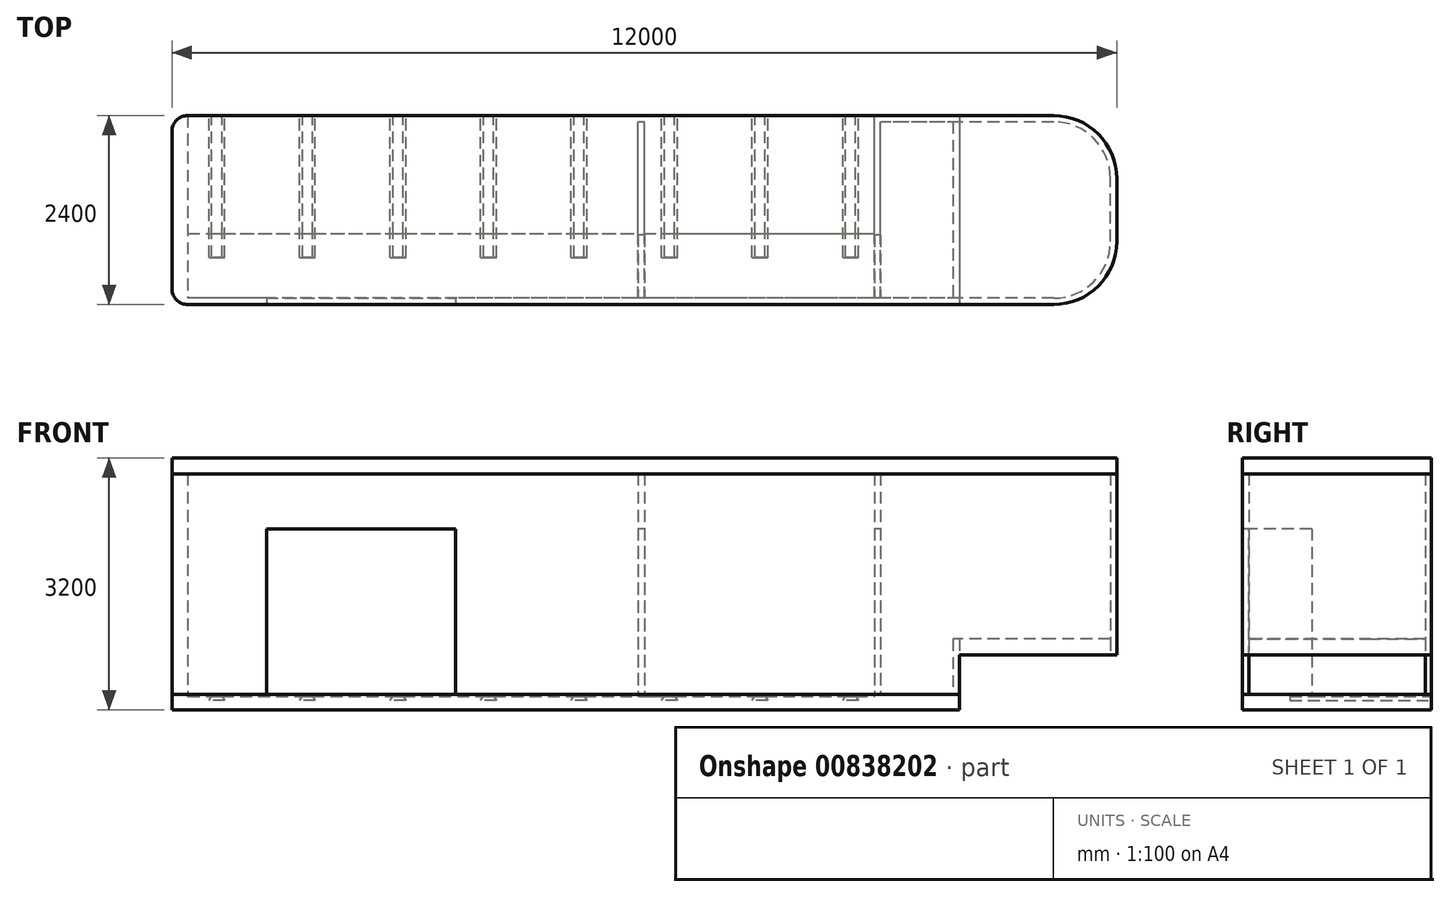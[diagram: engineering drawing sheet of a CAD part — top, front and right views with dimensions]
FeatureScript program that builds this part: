
annotation { "Feature Type Name" : "Feature", "Feature Type Description" : "" }
export const myFeature = defineFeature(function(context is Context, id is Id, definition is map)
    precondition{}
    {
        {
            var Q0;
            Q0=qCreatedBy(makeId("Top.planeOp"),FACE);
            var sketch = newSketch(context, id + "F0", { "sketchPlane" : qUnion([Q0])});
            skLineSegment(sketch, "E0.bottom", {"start": v(5200, -1200) * mm, "end": v(-5800, -1200) * mm});
            skLineSegment(sketch, "E0.top", {"start": v(5200, 1200) * mm, "end": v(2920, 1200) * mm});
            skLineSegment(sketch, "E0.left", {"start": v(6000, -400) * mm, "end": v(6000, 400) * mm});
            skLineSegment(sketch, "E0.right", {"start": v(-6000, -1000) * mm, "end": v(-6000, 1000) * mm});
            skPoint(sketch, "E0.middle", {"position": v(0, 0) * mm});
            skPoint(sketch, "E1.visualSharp", {"position": v(6000, 1200) * mm});
            skArc(sketch, "E1.filletArc", {"start": v(6000, 400) * mm, "mid": v(5765.69, 965.69) * mm, "end": v(5200, 1200) * mm});
            skPoint(sketch, "E2.visualSharp", {"position": v(6000, -1200) * mm});
            skArc(sketch, "E2.filletArc", {"start": v(5200, -1200) * mm, "mid": v(5765.69, -965.69) * mm, "end": v(6000, -400) * mm});
            skPoint(sketch, "E3.visualSharp", {"position": v(-6000, -1200) * mm});
            skArc(sketch, "E3.filletArc", {"start": v(-6000, -1000) * mm, "mid": v(-5941.42, -1141.42) * mm, "end": v(-5800, -1200) * mm});
            skPoint(sketch, "E4.visualSharp", {"position": v(-6000, 1200) * mm});
            skArc(sketch, "E4.filletArc", {"start": v(-5800, 1200) * mm, "mid": v(-5941.42, 1141.42) * mm, "end": v(-6000, 1000) * mm});
            skLineSegment(sketch, "E5", {"start": v(3000, -1120) * mm, "end": v(3000, 1120) * mm});
            skArc(sketch, "E6.0", {"start": v(5200, -1120) * mm, "mid": v(5709.12, -909.12) * mm, "end": v(5920, -400) * mm});
            skArc(sketch, "E6.1", {"start": v(5920, 400) * mm, "mid": v(5709.12, 909.12) * mm, "end": v(5200, 1120) * mm});
            skLineSegment(sketch, "E6.2", {"start": v(5200, 1120) * mm, "end": v(3000, 1120) * mm});
            skLineSegment(sketch, "E6.3", {"start": v(5920, -400) * mm, "end": v(5920, 400) * mm});
            skLineSegment(sketch, "E6.5", {"start": v(5200, -1120) * mm, "end": v(-5800, -1120) * mm});
            skLineSegment(sketch, "E7", {"start": v(-5800, 1200) * mm, "end": v(-5800, -1120) * mm});
            skLineSegment(sketch, "E8.0", {"start": v(2920, -1120) * mm, "end": v(2920, 1200) * mm});
            skLineSegment(sketch, "E9.0", {"start": v(0, -1120) * mm, "end": v(0, 1120) * mm});
            skLineSegment(sketch, "E10.0", {"start": v(-80, -1120) * mm, "end": v(-80, 1120) * mm});
            skLineSegment(sketch, "E11.trimOffspring", {"start": v(0, 1120) * mm, "end": v(-80, 1120) * mm});
            skLineSegment(sketch, "E12", {"start": v(-5800, 1200) * mm, "end": v(2920, 1200) * mm});
            skLineSegment(sketch, "E13.0", {"start": v(-5800, -300) * mm, "end": v(2920, -300) * mm});
            skLineSegment(sketch, "E14", {"start": v(4000, 1200) * mm, "end": v(4000, -1200) * mm});
            skLineSegment(sketch, "E15.0", {"start": v(3920, 1120) * mm, "end": v(3920, -1120) * mm});
            skSolve(sketch);
        }
        {
            var Q0;
            Q0=makeQuery(id+"F0.imprint","IMPRINT",FACE,{"disambiguationData":[TD([[makeQuery(id+"F0.imprint","IMPRINT",EDGE,{"derivedFrom":sQuery(id+"F0.wireOp",EDGE,"E0.bottom")}),-1.0]])]});
            var Q1;
            {var subQ0=sQuery(id+"F0.wireOp",EDGE,"E9.0");Q1=makeQuery(id+"F0.imprint","IMPRINT",FACE,{"disambiguationData":[TD([[makeQuery(id+"F0.imprint","IMPRINT",EDGE,{"derivedFrom":subQ0}),1.0]])]});}
            var Q2;
            {var subQ1=sQuery(id+"F0.wireOp",EDGE,"E5");Q2=makeQuery(id+"F0.imprint","IMPRINT",FACE,{"disambiguationData":[TD([[makeQuery(id+"F0.imprint","IMPRINT",EDGE,{"derivedFrom":subQ1}),1.0]])]});}
            var Q3;
            Q3=makeQuery(id+"F0.imprint","IMPRINT",FACE,{"disambiguationData":[TD([[makeQuery(id+"F0.imprint","IMPRINT",EDGE,{"derivedFrom":sQuery(id+"F0.wireOp",EDGE,"E0.right")}),-1.0]])]});
            extrude(context, id + "F1", {"entities" : qUnion([Q0, Q1, Q2, Q3]), "depth" : 2800 * mm, "offsetDistance" : 25 * mm});
        }
        {
            var Q0;
            {var subQ1=sQuery(id+"F0.wireOp",EDGE,"E5");Q0=makeQuery(id+"F0.imprint","IMPRINT",FACE,{"disambiguationData":[TD([[makeQuery(id+"F0.imprint","IMPRINT",EDGE,{"derivedFrom":subQ1}),-1.0]])]});}
            var Q1;
            {var subQ0=sQuery(id+"F0.wireOp",EDGE,"E9.0");Q1=makeQuery(id+"F0.imprint","IMPRINT",FACE,{"disambiguationData":[TD([[makeQuery(id+"F0.imprint","IMPRINT",EDGE,{"derivedFrom":subQ0}),1.0]])]});}
            var Q2;
            {var subQ0=sQuery(id+"F0.wireOp",EDGE,"E7");var subQ1=sQuery(id+"F0.wireOp",EDGE,"E6.5");var subQ2=makeQuery(id+"F0.imprint","INTERSECT",VERTEX,{"derivedFrom":[subQ1,subQ0]});Q2=makeQuery(id+"F0.imprint","IMPRINT",FACE,{"disambiguationData":[TD([[makeQuery(id+"F0.imprint","IMPRINT",EDGE,{"disambiguationData":[TD([[subQ2,1.0]])],"derivedFrom":subQ1}),-1.0]])]});}
            var Q3;
            {var subQ0=sQuery(id+"F0.wireOp",EDGE,"E8.0");var subQ1=sQuery(id+"F0.wireOp",EDGE,"E6.5");var subQ2=makeQuery(id+"F0.imprint","INTERSECT",VERTEX,{"derivedFrom":[subQ1,subQ0]});Q3=makeQuery(id+"F0.imprint","IMPRINT",FACE,{"disambiguationData":[TD([[makeQuery(id+"F0.imprint","IMPRINT",EDGE,{"disambiguationData":[TD([[subQ2,-1.0]])],"derivedFrom":subQ1}),-1.0]])]});}
            var Q4;
            {var subQ0=sQuery(id+"F0.wireOp",EDGE,"E11.trimOffspring");Q4=makeQuery(id+"F0.imprint","IMPRINT",FACE,{"disambiguationData":[TD([[makeQuery(id+"F0.imprint","IMPRINT",EDGE,{"derivedFrom":subQ0}),-1.0]])]});}
            var Q5;
            Q5=makeQuery(id+"F0.imprint","IMPRINT",FACE,{"disambiguationData":[TD([[makeQuery(id+"F0.imprint","IMPRINT",EDGE,{"derivedFrom":sQuery(id+"F0.wireOp",EDGE,"E0.right")}),-1.0]])]});
            var Q6;
            {var subQ1=sQuery(id+"F0.wireOp",EDGE,"E5");Q6=makeQuery(id+"F0.imprint","IMPRINT",FACE,{"disambiguationData":[TD([[makeQuery(id+"F0.imprint","IMPRINT",EDGE,{"derivedFrom":subQ1}),1.0]])]});}
            var Q7;
            {var subQ0=sQuery(id+"F0.wireOp",EDGE,"E15.0");Q7=makeQuery(id+"F0.imprint","IMPRINT",FACE,{"disambiguationData":[TD([[makeQuery(id+"F0.imprint","IMPRINT",EDGE,{"derivedFrom":subQ0}),1.0]])]});}
            extrude(context, id + "F2", {"entities" : qUnion([Q0, Q1, Q2, Q3, Q4, Q5, Q6, Q7]), "oppositeDirection" : true, "depth" : 200 * mm, "offsetDistance" : 25 * mm});
        }
        {
            var Q0;
            Q0=makeQuery(id+"F1.opExtrude","SWEPT_FACE",FACE,{"disambiguationData":[OSD([sQuery(id+"F0.wireOp",EDGE,"E0.bottom")])]});
            var sketch = newSketch(context, id + "F3", { "sketchPlane" : qUnion([Q0])});
            skLineSegment(sketch, "E16.bottom", {"start": v(-4800, 0) * mm, "end": v(-2400, 0) * mm});
            skLineSegment(sketch, "E16.top", {"start": v(-4800, 2100) * mm, "end": v(-2400, 2100) * mm});
            skLineSegment(sketch, "E16.left", {"start": v(-4800, 0) * mm, "end": v(-4800, 2100) * mm});
            skLineSegment(sketch, "E16.right", {"start": v(-2400, 0) * mm, "end": v(-2400, 2100) * mm});
            skSolve(sketch);
        }
        {
            var Q0;
            Q0=makeQuery(id+"F3.imprint","IMPRINT",FACE,{"disambiguationData":[TD([[makeQuery(id+"F3.imprint","IMPRINT",EDGE,{"derivedFrom":sQuery(id+"F3.wireOp",EDGE,"E16.bottom")}),-1.0]])]});
            extrude(context, id + "F4", {"entities" : qUnion([Q0]), "operationType" : NewBodyOperationType.REMOVE, "oppositeDirection" : true, "depth" : 1454.27 * mm, "offsetDistance" : 25 * mm});
        }
        {
            var Q0;
            Q0=makeQuery(id+"F1.opExtrude","SWEPT_FACE",FACE,{"disambiguationData":[OSD([sQuery(id+"F0.wireOp",EDGE,"E10.0")])]});
            var sketch = newSketch(context, id + "F5", { "sketchPlane" : qUnion([Q0])});
            skLineSegment(sketch, "E17.bottom", {"start": v(320, 2100) * mm, "end": v(1120, 2100) * mm});
            skLineSegment(sketch, "E17.top", {"start": v(320, 0) * mm, "end": v(1120, 0) * mm});
            skLineSegment(sketch, "E17.left", {"start": v(320, 2100) * mm, "end": v(320, 0) * mm});
            skLineSegment(sketch, "E17.right", {"start": v(1120, 2100) * mm, "end": v(1120, 0) * mm});
            skSolve(sketch);
        }
        {
            var Q0;
            Q0=makeQuery(id+"F5.imprint","IMPRINT",FACE,{"disambiguationData":[TD([[makeQuery(id+"F5.imprint","IMPRINT",EDGE,{"derivedFrom":sQuery(id+"F5.wireOp",EDGE,"E17.bottom")}),-1.0]])]});
            extrude(context, id + "F6", {"entities" : qUnion([Q0]), "operationType" : NewBodyOperationType.REMOVE, "oppositeDirection" : true, "depth" : 3837 * mm, "offsetDistance" : 25 * mm});
        }
        {
            var Q0;
            {var subQ0=sQuery(id+"F0.wireOp",EDGE,"E11.trimOffspring");Q0=makeQuery(id+"F0.imprint","IMPRINT",FACE,{"disambiguationData":[TD([[makeQuery(id+"F0.imprint","IMPRINT",EDGE,{"derivedFrom":subQ0}),-1.0]])]});}
            extrude(context, id + "F7", {"entities" : qUnion([Q0]), "operationType" : NewBodyOperationType.REMOVE, "oppositeDirection" : true, "depth" : 30 * mm, "offsetDistance" : 25 * mm});
        }
        {
            var Q0;
            Q0=makeQuery(id+"F2.opExtrude","SWEPT_FACE",FACE,{"disambiguationData":[OSD([sQuery(id+"F0.wireOp",EDGE,"E0.top"),sQuery(id+"F0.wireOp",EDGE,"E12")])]});
            var sketch = newSketch(context, id + "F8", { "sketchPlane" : qUnion([Q0])});
            skLineSegment(sketch, "E18", {"start": v(-2920, -200) * mm, "end": v(5800, -200) * mm});
            skLineSegment(sketch, "E19", {"start": v(-2920, -200) * mm, "end": v(-2920, -30) * mm});
            skLineSegment(sketch, "E20", {"start": v(-2920, -30) * mm, "end": v(5800, -30) * mm});
            skLineSegment(sketch, "E21", {"start": v(5800, -30) * mm, "end": v(5800, -200) * mm});
            skLineSegment(sketch, "E22", {"start": v(-2684.32, -30) * mm, "end": v(-2720, -80) * mm});
            skLineSegment(sketch, "E23", {"start": v(-2720, -80) * mm, "end": v(-2520, -80) * mm});
            skLineSegment(sketch, "E24", {"start": v(-2520, -80) * mm, "end": v(-2555.68, -30) * mm});
            skLineSegment(sketch, "E25.1.0.0", {"start": v(-1534.32, -30) * mm, "end": v(-1570, -80) * mm});
            skLineSegment(sketch, "E25.1.0.1", {"start": v(-1570, -80) * mm, "end": v(-1370, -80) * mm});
            skLineSegment(sketch, "E25.1.0.2", {"start": v(-1370, -80) * mm, "end": v(-1405.68, -30) * mm});
            skLineSegment(sketch, "E25.2.0.0", {"start": v(-384.32, -30) * mm, "end": v(-420, -80) * mm});
            skLineSegment(sketch, "E25.2.0.1", {"start": v(-420, -80) * mm, "end": v(-220, -80) * mm});
            skLineSegment(sketch, "E25.2.0.2", {"start": v(-220, -80) * mm, "end": v(-255.68, -30) * mm});
            skLineSegment(sketch, "E25.3.0.0", {"start": v(765.68, -30) * mm, "end": v(730, -80) * mm});
            skLineSegment(sketch, "E25.3.0.1", {"start": v(730, -80) * mm, "end": v(930, -80) * mm});
            skLineSegment(sketch, "E25.3.0.2", {"start": v(930, -80) * mm, "end": v(894.32, -30) * mm});
            skLineSegment(sketch, "E25.4.0.0", {"start": v(1915.68, -30) * mm, "end": v(1880, -80) * mm});
            skLineSegment(sketch, "E25.4.0.1", {"start": v(1880, -80) * mm, "end": v(2080, -80) * mm});
            skLineSegment(sketch, "E25.4.0.2", {"start": v(2080, -80) * mm, "end": v(2044.32, -30) * mm});
            skLineSegment(sketch, "E25.5.0.0", {"start": v(3065.68, -30) * mm, "end": v(3030, -80) * mm});
            skLineSegment(sketch, "E25.5.0.1", {"start": v(3030, -80) * mm, "end": v(3230, -80) * mm});
            skLineSegment(sketch, "E25.5.0.2", {"start": v(3230, -80) * mm, "end": v(3194.32, -30) * mm});
            skLineSegment(sketch, "E25.6.0.0", {"start": v(4215.68, -30) * mm, "end": v(4180, -80) * mm});
            skLineSegment(sketch, "E25.6.0.1", {"start": v(4180, -80) * mm, "end": v(4380, -80) * mm});
            skLineSegment(sketch, "E25.6.0.2", {"start": v(4380, -80) * mm, "end": v(4344.32, -30) * mm});
            skLineSegment(sketch, "E25.7.0.0", {"start": v(5365.68, -30) * mm, "end": v(5330, -80) * mm});
            skLineSegment(sketch, "E25.7.0.1", {"start": v(5330, -80) * mm, "end": v(5530, -80) * mm});
            skLineSegment(sketch, "E25.7.0.2", {"start": v(5530, -80) * mm, "end": v(5494.32, -30) * mm});
            skLineSegment(sketch, "E25.direction1", {"start": v(-2720, -80) * mm, "end": v(-1570, -80) * mm, "construction": true});
            skSolve(sketch);
        }
        {
            var Q0;
            {var subQ0=sQuery(id+"F8.wireOp",EDGE,"E22");Q0=makeQuery(id+"F8.imprint","IMPRINT",FACE,{"disambiguationData":[TD([[makeQuery(id+"F8.imprint","IMPRINT",EDGE,{"derivedFrom":subQ0}),1.0]])]});}
            var Q1;
            {var subQ0=sQuery(id+"F8.wireOp",EDGE,"E25.1.0.0");Q1=makeQuery(id+"F8.imprint","IMPRINT",FACE,{"disambiguationData":[TD([[makeQuery(id+"F8.imprint","IMPRINT",EDGE,{"derivedFrom":subQ0}),1.0]])]});}
            var Q2;
            {var subQ0=sQuery(id+"F8.wireOp",EDGE,"E25.2.0.0");Q2=makeQuery(id+"F8.imprint","IMPRINT",FACE,{"disambiguationData":[TD([[makeQuery(id+"F8.imprint","IMPRINT",EDGE,{"derivedFrom":subQ0}),1.0]])]});}
            var Q3;
            {var subQ0=sQuery(id+"F8.wireOp",EDGE,"E25.4.0.0");Q3=makeQuery(id+"F8.imprint","IMPRINT",FACE,{"disambiguationData":[TD([[makeQuery(id+"F8.imprint","IMPRINT",EDGE,{"derivedFrom":subQ0}),1.0]])]});}
            var Q4;
            {var subQ0=sQuery(id+"F8.wireOp",EDGE,"E25.3.0.0");Q4=makeQuery(id+"F8.imprint","IMPRINT",FACE,{"disambiguationData":[TD([[makeQuery(id+"F8.imprint","IMPRINT",EDGE,{"derivedFrom":subQ0}),1.0]])]});}
            var Q5;
            {var subQ0=sQuery(id+"F8.wireOp",EDGE,"E25.5.0.0");Q5=makeQuery(id+"F8.imprint","IMPRINT",FACE,{"disambiguationData":[TD([[makeQuery(id+"F8.imprint","IMPRINT",EDGE,{"derivedFrom":subQ0}),1.0]])]});}
            var Q6;
            {var subQ0=sQuery(id+"F8.wireOp",EDGE,"E25.6.0.0");Q6=makeQuery(id+"F8.imprint","IMPRINT",FACE,{"disambiguationData":[TD([[makeQuery(id+"F8.imprint","IMPRINT",EDGE,{"derivedFrom":subQ0}),1.0]])]});}
            var Q7;
            {var subQ0=sQuery(id+"F8.wireOp",EDGE,"E25.7.0.0");Q7=makeQuery(id+"F8.imprint","IMPRINT",FACE,{"disambiguationData":[TD([[makeQuery(id+"F8.imprint","IMPRINT",EDGE,{"derivedFrom":subQ0}),1.0]])]});}
            extrude(context, id + "F9", {"entities" : qUnion([Q0, Q1, Q2, Q3, Q4, Q5, Q6, Q7]), "operationType" : NewBodyOperationType.REMOVE, "oppositeDirection" : true, "depth" : 1800 * mm, "offsetDistance" : 25 * mm});
        }
        {
            var Q0;
            Q0=makeQuery(id+"F0.imprint","IMPRINT",FACE,{"disambiguationData":[TD([[makeQuery(id+"F0.imprint","IMPRINT",EDGE,{"derivedFrom":sQuery(id+"F0.wireOp",EDGE,"E0.left")}),1.0]])]});
            extrude(context, id + "F10", {"entities" : qUnion([Q0]), "operationType" : NewBodyOperationType.REMOVE, "depth" : 500 * mm, "offsetDistance" : 25 * mm});
        }
        {
            var Q0;
            {var subQ0=sQuery(id+"F0.wireOp",EDGE,"E15.0");Q0=makeQuery(id+"F0.imprint","IMPRINT",FACE,{"disambiguationData":[TD([[makeQuery(id+"F0.imprint","IMPRINT",EDGE,{"derivedFrom":subQ0}),1.0]])]});}
            extrude(context, id + "F11", {"entities" : qUnion([Q0]), "depth" : 700 * mm, "offsetDistance" : 25 * mm});
        }
        {
            var Q0;
            Q0=makeQuery(id+"F10.boolean.opBoolean","COPY",FACE,{"derivedFrom":makeQuery(id+"F10.opExtrude","CAP_FACE",FACE,{"disambiguationData":[OSD([sQuery(id+"F0.wireOp",EDGE,"E0.bottom"),sQuery(id+"F0.wireOp",EDGE,"E0.top"),sQuery(id+"F0.wireOp",EDGE,"E0.left"),sQuery(id+"F0.wireOp",EDGE,"E1.filletArc"),sQuery(id+"F0.wireOp",EDGE,"E2.filletArc"),sQuery(id+"F0.wireOp",EDGE,"E6.0"),sQuery(id+"F0.wireOp",EDGE,"E6.1"),sQuery(id+"F0.wireOp",EDGE,"E6.2"),sQuery(id+"F0.wireOp",EDGE,"E6.3"),sQuery(id+"F0.wireOp",EDGE,"E6.5"),sQuery(id+"F0.wireOp",EDGE,"E14")])],"isStart":false})});
            var sketch = newSketch(context, id + "F12", { "sketchPlane" : qUnion([Q0])});
            skLineSegment(sketch, "E26", {"start": v(4000, -1120) * mm, "end": v(4000, 1120) * mm});
            skSolve(sketch);
        }
        {
            var Q0;
            Q0=makeQuery(id+"F12.imprint","IMPRINT",FACE,{"disambiguationData":[TD([[makeQuery(id+"F12.imprint","IMPRINT",EDGE,{"derivedFrom":sQuery(id+"F12.wireOp",EDGE,"E26")}),-1.0]])]});
            extrude(context, id + "F13", {"entities" : qUnion([Q0]), "oppositeDirection" : true, "depth" : 200 * mm, "offsetDistance" : 25 * mm});
        }
        {
            var Q0;
            Q0=makeQuery(id+"F1.opExtrude","CAP_FACE",FACE,{"disambiguationData":[OSD([sQuery(id+"F0.wireOp",EDGE,"E0.bottom"),sQuery(id+"F0.wireOp",EDGE,"E0.top"),sQuery(id+"F0.wireOp",EDGE,"E0.left"),sQuery(id+"F0.wireOp",EDGE,"E0.right"),sQuery(id+"F0.wireOp",EDGE,"E1.filletArc"),sQuery(id+"F0.wireOp",EDGE,"E2.filletArc"),sQuery(id+"F0.wireOp",EDGE,"E3.filletArc"),sQuery(id+"F0.wireOp",EDGE,"E4.filletArc"),sQuery(id+"F0.wireOp",EDGE,"E5"),sQuery(id+"F0.wireOp",EDGE,"E6.0"),sQuery(id+"F0.wireOp",EDGE,"E6.1"),sQuery(id+"F0.wireOp",EDGE,"E6.2"),sQuery(id+"F0.wireOp",EDGE,"E6.3"),sQuery(id+"F0.wireOp",EDGE,"E6.5"),sQuery(id+"F0.wireOp",EDGE,"E7"),sQuery(id+"F0.wireOp",EDGE,"E8.0"),sQuery(id+"F0.wireOp",EDGE,"E9.0"),sQuery(id+"F0.wireOp",EDGE,"E10.0"),sQuery(id+"F0.wireOp",EDGE,"E11.trimOffspring")])],"isStart":false});
            var sketch = newSketch(context, id + "F14", { "sketchPlane" : qUnion([Q0])});
            skLineSegment(sketch, "E27.bottom", {"start": v(5200, -1200) * mm, "end": v(-5800, -1200) * mm});
            skLineSegment(sketch, "E27.top", {"start": v(5200, 1200) * mm, "end": v(2920, 1200) * mm});
            skLineSegment(sketch, "E27.left", {"start": v(6000, -400) * mm, "end": v(6000, 400) * mm});
            skLineSegment(sketch, "E27.right", {"start": v(-6000, -1000) * mm, "end": v(-6000, 1000) * mm});
            skPoint(sketch, "E28.visualSharp", {"position": v(6000, 1200) * mm});
            skArc(sketch, "E28.filletArc", {"start": v(6000, 400) * mm, "mid": v(5765.69, 965.69) * mm, "end": v(5200, 1200) * mm});
            skPoint(sketch, "E29.visualSharp", {"position": v(6000, -1200) * mm});
            skArc(sketch, "E29.filletArc", {"start": v(5200, -1200) * mm, "mid": v(5765.69, -965.69) * mm, "end": v(6000, -400) * mm});
            skPoint(sketch, "E30.visualSharp", {"position": v(-6000, -1200) * mm});
            skArc(sketch, "E30.filletArc", {"start": v(-6000, -1000) * mm, "mid": v(-5941.42, -1141.42) * mm, "end": v(-5800, -1200) * mm});
            skPoint(sketch, "E31.visualSharp", {"position": v(-6000, 1200) * mm});
            skArc(sketch, "E31.filletArc", {"start": v(-5800, 1200) * mm, "mid": v(-5941.42, 1141.42) * mm, "end": v(-6000, 1000) * mm});
            skLineSegment(sketch, "E32", {"start": v(-5800, 1200) * mm, "end": v(2920, 1200) * mm});
            skSolve(sketch);
        }
        {
            var Q0;
            Q0=makeQuery(id+"F14.imprint","IMPRINT",FACE,{"disambiguationData":[TD([[makeQuery(id+"F14.imprint","IMPRINT",EDGE,{"derivedFrom":sQuery(id+"F14.wireOp",EDGE,"E27.bottom")}),-1.0]])]});
            var Q1;
            {var subQ1=sQuery(id+"F0.wireOp",EDGE,"E5");Q1=makeQuery(id+"F14.imprint","IMPRINT",FACE,{"disambiguationData":[TD([[makeQuery(id+"F14.imprint","IMPRINT",EDGE,{"derivedFrom":makeQuery(id+"F1.opExtrude","CAP_EDGE",EDGE,{"disambiguationData":[OSD([subQ1])],"isStart":false})}),-1.0]])]});}
            var Q2;
            Q2=makeQuery(id+"F14.imprint","IMPRINT",FACE,{"disambiguationData":[TD([[makeQuery(id+"F14.imprint","IMPRINT",EDGE,{"derivedFrom":sQuery(id+"F14.wireOp",EDGE,"E32")}),-1.0]])]});
            extrude(context, id + "F15", {"entities" : qUnion([Q0, Q1, Q2]), "depth" : 200 * mm, "offsetDistance" : 25 * mm});
        }
    });
